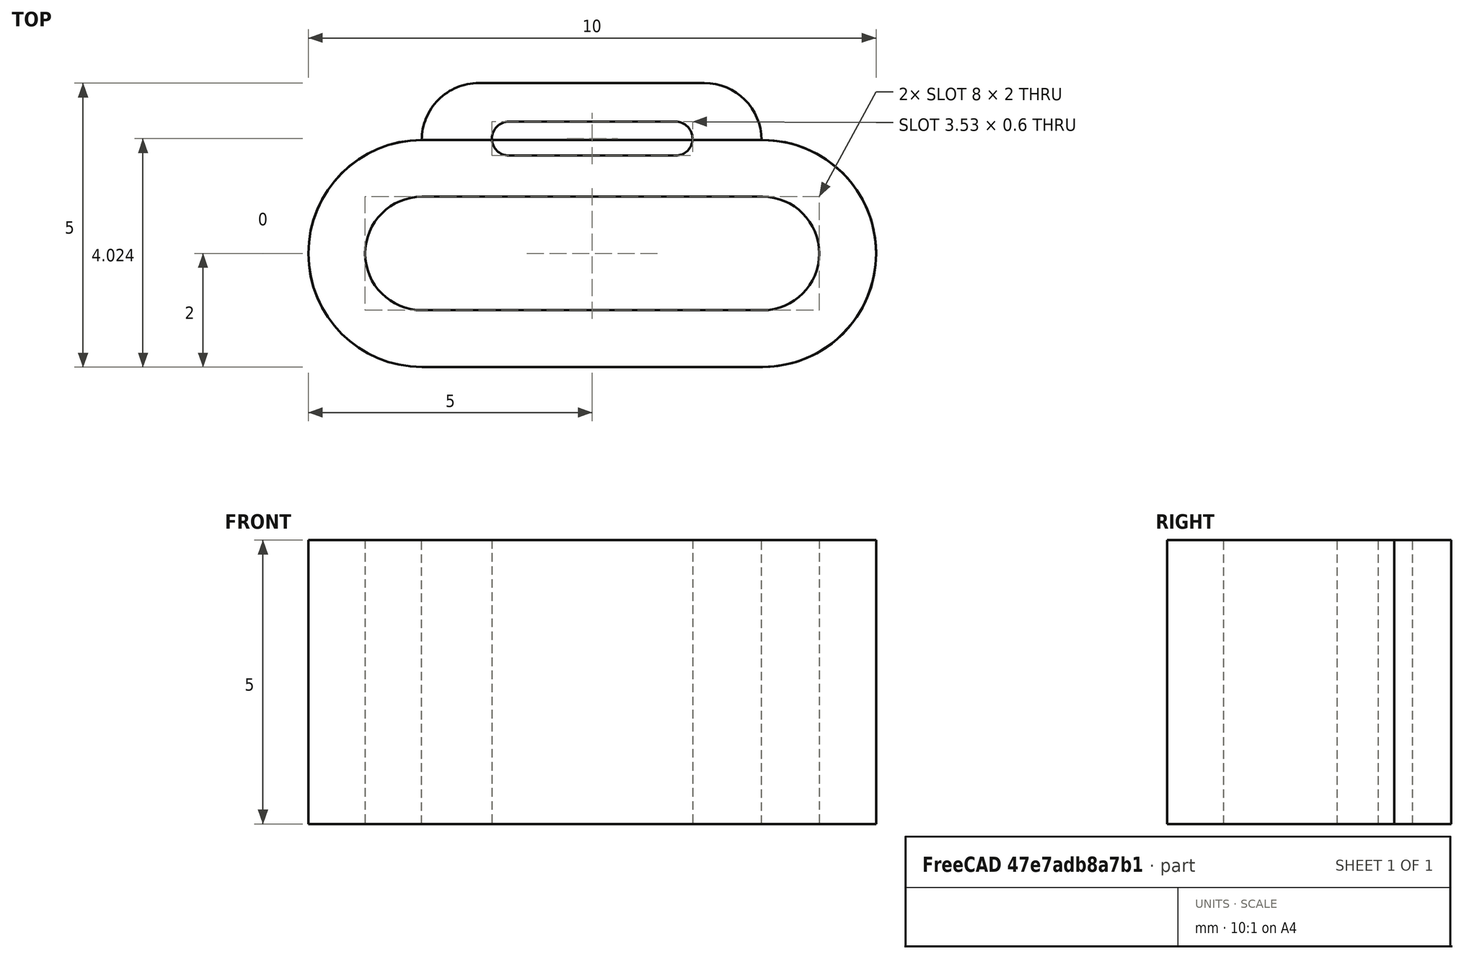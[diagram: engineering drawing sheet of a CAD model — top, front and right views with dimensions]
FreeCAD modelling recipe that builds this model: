
FCSTD DOCUMENT  (FreeCAD 2024.1R35694 (Git))
Label: strap_holder
License: Creative Commons Attribution 4.0
LicenseURL: https://creativecommons.org/licenses/by/4.0/
objects: TechDraw::DrawViewDimension×5, TechDraw::DrawProjGroupItem×3, Sketcher::SketchObject×2, PartDesign::Pad×2, PartDesign::Body×2, Spreadsheet::Sheet×1, TechDraw::DrawSVGTemplate×1, TechDraw::DrawViewImage×1, TechDraw::DrawProjGroup×1, TechDraw::DrawViewSpreadsheet×1, TechDraw::DrawPage×1
note: 15 computed .brp shape members not serialized (recipe doc carries the construction recipe); baked Part::Feature solids carry a one-line shape summary decoded from their .brp

FEATURE [Sketcher::SketchObject] Sketch
  FullyConstrained = true
  MapMode = 5
  Support = -> [XY_Plane]
  expr: Constraints[11] = <<parameters>>.hole_radius
  expr: Constraints[12] = <<parameters>>.thickness
  expr: Constraints[16] = <<parameters>>.hole_length
  sketch-geometry (8):
    g0: ArcOfCircle CenterX=-3 CenterY=0 CenterZ=0 NormalX=0 NormalY=0 NormalZ=1 AngleXU=0 Radius=1 StartAngle=1.5708 EndAngle=4.71239
    g1: ArcOfCircle CenterX=3 CenterY=1e-16 CenterZ=0 NormalX=0 NormalY=0 NormalZ=1 AngleXU=0 Radius=1 StartAngle=4.71239 EndAngle=7.85398
    g2: LineSegment StartX=-3 StartY=-1 StartZ=0 EndX=3 EndY=-1 EndZ=0
    g3: LineSegment StartX=3 StartY=1 StartZ=0 EndX=-3 EndY=1 EndZ=0
    g4: ArcOfCircle CenterX=-3 CenterY=2e-16 CenterZ=0 NormalX=0 NormalY=0 NormalZ=1 AngleXU=0 Radius=2 StartAngle=1.5708 EndAngle=4.71239
    g5: ArcOfCircle CenterX=3 CenterY=1e-16 CenterZ=0 NormalX=0 NormalY=0 NormalZ=1 AngleXU=0 Radius=2 StartAngle=4.71239 EndAngle=7.85398
    g6: LineSegment StartX=-3 StartY=-2 StartZ=0 EndX=3 EndY=-2 EndZ=0
    g7: LineSegment StartX=3 StartY=2 StartZ=0 EndX=-3 EndY=2 EndZ=0
  constraints (17):
    c: Tangent(g0,g2) = -1.5708
    c: Tangent(g2,g1) = -1.5708
    c: Tangent(g1,g3) = -1.5708
    c: Tangent(g3,g0) = -1.5708
    c: Equal(g0,g1)
    c: PointOnObject(g0,g-1)
    c: Tangent(g4,g6) = -1.5708
    c: Tangent(g6,g5) = -1.5708
    c: Tangent(g5,g7) = -1.5708
    c: Tangent(g7,g4) = -1.5708
    c: Equal(g4,g5)
    c: Radius(g0) = 1
    c: DistanceY(g1,g5) = 1
    c: Symmetric(g5,g4,g-2)
    c: Symmetric(g1,g0,g-2)
    c: Coincident(g5,g1)
    c: DistanceX(g6,g6) = 6
FEATURE [PartDesign::Pad] Pad
  Direction = (0,0,1)
  Length = 5
  Length2 = 10
  Profile = -> Sketch
  ReferenceAxis = -> Sketch [N_Axis]
  Type = 0
  expr: Length = <<parameters>>.height
FEATURE [PartDesign::Body] Body  label="single"
  Group = -> [Sketch,Pad]
  Origin = -> Origin
  Tip = -> Pad
FEATURE [Spreadsheet::Sheet] Spreadsheet  label="parameters"
  cells = A1='Parameter; B1='Value; A2='thickness; B2(thickness)==1 mm; A3='hole_radius; B3(hole_radius)==1 mm; A4='hole_length; B4(hole_length)==6 mm; A5='height; B5(height)==5 mm
FEATURE [TechDraw::DrawSVGTemplate] Template
  EditableTexts = Designed_by_Name=Dennis Wittchen; Drawing_number=1; FC-Date=Jan 17 2024; FC-SC=3:1; FC-SH=1; FC-Title=strap holder; Subtitle=modular system
  Height = 210
  Orientation = 1
  Template = /Applications/FreeCAD.app/Contents/Resources/share/Mod/TechDraw/Templates/A4_LandscapeTD.svg
  Width = 297
FEATURE [TechDraw::DrawViewImage] ActiveView
  Height = 30
  ImageFile = <userpath>/Library/Caches/FreeCAD/Cache/FreeCAD_Doc_b2a2b77d-9e3d-4a47-8089-e41d462fed02_9dbf0a_21681/PageActiveViewkthZav.png
  LockPosition = false
  Rotation = 0
  Scale = 0.3
  ScaleType = 2
  Width = 30
  X = 165.254
  Y = 128.537
FEATURE [TechDraw::DrawProjGroupItem] ProjItem  label="Front"
  CoarseView = false
  Direction = (0,-1,0)
  Focus = 100
  HardHidden = false
  IsoCount = 0
  IsoHidden = false
  IsoVisible = false
  LockPosition = true
  Perspective = false
  Rotation = 0
  RotationVector = (1,0,1e-06)
  Scale = 4
  ScaleType = 2
  ScrubCount = 0
  SeamHidden = false
  SeamVisible = false
  SmoothHidden = false
  SmoothVisible = true
  Source = -> [Body]
  Type = 0
  X = 0
  XDirection = (1,0,1e-06)
  Y = 0
FEATURE [TechDraw::DrawProjGroupItem] ProjItem001  label="Top"
  CoarseView = false
  Direction = (-1e-06,0,1)
  Focus = 100
  HardHidden = false
  IsoCount = 0
  IsoHidden = false
  IsoVisible = false
  LockPosition = false
  Perspective = false
  Rotation = 0
  RotationVector = (1,0,0)
  ScaleType = 2
  ScrubCount = 0
  SeamHidden = false
  SeamVisible = false
  SmoothHidden = false
  SmoothVisible = true
  Source = -> [Body]
  Type = 4
  X = 0
  XDirection = (1,0,1e-06)
  Y = -43
FEATURE [TechDraw::DrawProjGroupItem] ProjItem002  label="Bottom"
  CoarseView = false
  Direction = (1e-06,0,-1)
  Focus = 100
  HardHidden = false
  IsoCount = 0
  IsoHidden = false
  IsoVisible = false
  LockPosition = false
  Perspective = false
  Rotation = 0
  RotationVector = (1,0,0)
  ScaleType = 2
  ScrubCount = 0
  SeamHidden = false
  SeamVisible = false
  SmoothHidden = false
  SmoothVisible = true
  Source = -> [Body]
  Type = 5
  X = 0
  XDirection = (1,0,1e-06)
  Y = 43
FEATURE [TechDraw::DrawProjGroup] ProjGroup
  Anchor = -> ProjItem
  AutoDistribute = true
  LockPosition = false
  ProjectionType = 0
  Rotation = 0
  Scale = 4
  ScaleType = 2
  Source = -> [Body]
  Views = -> [ProjItem,ProjItem001,ProjItem002]
  X = 79.4396
  Y = 129.966
  spacingX = 25
  spacingY = 25
FEATURE [TechDraw::DrawViewDimension] Dimension
  AngleOverride = false
  Arbitrary = false
  ArbitraryTolerances = false
  EqualTolerance = true
  ExtensionAngle = 0
  FormatSpec = R%.2w
  FormatSpecOverTolerance = %+.2w
  FormatSpecUnderTolerance = %+.2w
  Inverted = false
  LineAngle = 0
  LockPosition = false
  MeasureType = 1
  OverTolerance = 0
  References2D = -> [ProjItem002]
  Rotation = 0
  ScaleType = 0
  TheoreticalExact = false
  Type = 4
  UnderTolerance = 0
  X = -28.2438
  Y = 19.9944
FEATURE [TechDraw::DrawViewDimension] Dimension001
  AngleOverride = false
  Arbitrary = false
  ArbitraryTolerances = false
  EqualTolerance = true
  ExtensionAngle = 0
  FormatSpec = %.2w
  FormatSpecOverTolerance = %+.2w
  FormatSpecUnderTolerance = %+.2w
  Inverted = false
  LineAngle = 0
  LockPosition = false
  MeasureType = 1
  OverTolerance = 0
  References2D = -> [ProjItem001]
  Rotation = 0
  ScaleType = 0
  TheoreticalExact = false
  Type = 1
  UnderTolerance = 0
  X = -0.524319
  Y = 18.8893
FEATURE [TechDraw::DrawViewDimension] Dimension002
  AngleOverride = false
  Arbitrary = false
  ArbitraryTolerances = false
  EqualTolerance = true
  ExtensionAngle = 0
  FormatSpec = %.2w
  FormatSpecOverTolerance = %+.2w
  FormatSpecUnderTolerance = %+.2w
  Inverted = false
  LineAngle = 0
  LockPosition = false
  MeasureType = 1
  OverTolerance = 0
  References2D = -> [ProjItem002]
  Rotation = 0
  ScaleType = 0
  TheoreticalExact = false
  Type = 0
  UnderTolerance = 0
  X = 26.6812
  Y = -9.61717
FEATURE [TechDraw::DrawViewDimension] Dimension003
  AngleOverride = false
  Arbitrary = false
  ArbitraryTolerances = false
  EqualTolerance = true
  ExtensionAngle = 0
  FormatSpec = %.2w
  FormatSpecOverTolerance = %+.2w
  FormatSpecUnderTolerance = %+.2w
  Inverted = false
  LineAngle = 0
  LockPosition = false
  MeasureType = 1
  OverTolerance = 0
  References2D = -> [ProjItem]
  Rotation = 0
  ScaleType = 0
  TheoreticalExact = false
  Type = 2
  UnderTolerance = 0
  X = 26.9911
  Y = 2.67476
FEATURE [TechDraw::DrawViewSpreadsheet] Sheet
  CellEnd = B5
  CellStart = A1
  Font = osifont
  LineWidth = 0.35
  LockPosition = false
  Rotation = 0
  ScaleType = 2
  Source = -> Spreadsheet
  Symbol = <blob: 2375 chars omitted>
  TextSize = 12
  X = 244.081
  Y = 126.619
FEATURE [TechDraw::DrawViewDimension] Dimension004
  AngleOverride = false
  Arbitrary = false
  ArbitraryTolerances = false
  EqualTolerance = true
  ExtensionAngle = 0
  FormatSpec = %.2w
  FormatSpecOverTolerance = %+.2w
  FormatSpecUnderTolerance = %+.2w
  Inverted = false
  LineAngle = 0
  LockPosition = false
  MeasureType = 1
  OverTolerance = 0
  References2D = -> [ProjItem]
  Rotation = 0
  ScaleType = 0
  TheoreticalExact = false
  Type = 1
  UnderTolerance = 0
  X = -1.0067
  Y = 19.151
FEATURE [TechDraw::DrawPage] Page  label="documentation"
  KeepUpdated = true
  NextBalloonIndex = 1
  ProjectionType = 0
  Template = -> Template
  Views = -> [ActiveView,ProjGroup,Dimension,Dimension001,Dimension002,Dimension003,Sheet,Dimension004]
FEATURE [Sketcher::SketchObject] Sketch001
  FullyConstrained = false
  MapMode = 5
  Support = -> [XY_Plane001]
  expr: Constraints[13] = <<parameters>>.hole_length
  expr: Constraints[9] = <<parameters>>.hole_radius
  sketch-geometry (14):
    g0: ArcOfCircle CenterX=-3 CenterY=0 CenterZ=0 NormalX=0 NormalY=0 NormalZ=1 AngleXU=0 Radius=1 StartAngle=1.5708 EndAngle=4.71239
    g1: ArcOfCircle CenterX=3 CenterY=0 CenterZ=0 NormalX=0 NormalY=0 NormalZ=1 AngleXU=0 Radius=1 StartAngle=4.71239 EndAngle=7.85398
    g2: LineSegment StartX=-3 StartY=-1 StartZ=0 EndX=3 EndY=-1 EndZ=0
    g3: LineSegment StartX=3 StartY=1 StartZ=0 EndX=-3 EndY=1 EndZ=0
    g4: ArcOfCircle CenterX=-3 CenterY=1e-16 CenterZ=0 NormalX=0 NormalY=0 NormalZ=1 AngleXU=0 Radius=1.99883 StartAngle=1.5722 EndAngle=4.71239
    g5: ArcOfCircle CenterX=3 CenterY=0 CenterZ=0 NormalX=0 NormalY=0 NormalZ=1 AngleXU=0 Radius=1.99883 StartAngle=4.71239 EndAngle=7.86247
    g6: LineSegment StartX=-3 StartY=-1.99883 StartZ=0 EndX=3 EndY=-1.99883 EndZ=0
    g7: ArcOfCircle CenterX=-1.46614 CenterY=2.02372 CenterZ=0 NormalX=0 NormalY=0 NormalZ=1 AngleXU=0 Radius=0.3 StartAngle=1.5708 EndAngle=4.71239
    g8: ArcOfCircle CenterX=1.46614 CenterY=2.02372 CenterZ=0 NormalX=0 NormalY=0 NormalZ=1 AngleXU=0 Radius=0.3 StartAngle=4.71239 EndAngle=7.85398
    g9: LineSegment StartX=-1.46614 StartY=2.32372 StartZ=0 EndX=1.46614 EndY=2.32372 EndZ=0
    g10: LineSegment StartX=-1.46614 StartY=1.72372 StartZ=0 EndX=1.46614 EndY=1.72372 EndZ=0
    g11: ArcOfCircle CenterX=-2 CenterY=2.00024 CenterZ=0 NormalX=0 NormalY=0 NormalZ=1 AngleXU=0 Radius=1.00281 StartAngle=1.5708 EndAngle=3.143
    g12: LineSegment StartX=-2 StartY=3.00306 StartZ=0 EndX=1.97343 EndY=3.00306 EndZ=0
    g13: ArcOfCircle CenterX=1.97343 CenterY=1.99343 CenterZ=0 NormalX=0 NormalY=0 NormalZ=1 AngleXU=0 Radius=1.00963 StartAngle=0.00527808 EndAngle=1.5708
  constraints (26):
    c: Tangent(g0,g2) = -1.5708
    c: Tangent(g2,g1) = -1.5708
    c: Tangent(g1,g3) = -1.5708
    c: Tangent(g3,g0) = -1.5708
    c: Equal(g0,g1)
    c: PointOnObject(g0,g-1)
    c: Tangent(g4,g6) = -1.5708
    c: Tangent(g6,g5) = -1.5708
    c: Equal(g4,g5)
    c: Radius(g0) = 1
    c: Symmetric(g5,g4,g-2)
    c: Symmetric(g1,g0,g-2)
    c: Coincident(g5,g1)
    c: DistanceX(g6,g6) = 6
    c: Tangent(g7,g9) = 1.5708
    c: Tangent(g7,g10) = -1.5708
    c: Tangent(g8,g9) = 1.5708
    c: Tangent(g8,g10) = -1.5708
    c: Equal(g7,g8)
    c: Radius(g7) = 0.3
    c: Symmetric(g7,g8,g-2)
    c: Perpendicular(g4,g11) = 1.5708
    c: Tangent(g11,g12) = 1.5708
    c: Tangent(g12,g13) = 1.5708
    c: Coincident(g13,g5)
    c: Horizontal(g12)
FEATURE [PartDesign::Pad] Pad001
  Direction = (0,0,1)
  Length = 5
  Length2 = 10
  Profile = -> Sketch001
  ReferenceAxis = -> Sketch001 [N_Axis]
  Refine = true
  Type = 0
  expr: Length = <<parameters>>.height
FEATURE [PartDesign::Body] Body001  label="double"
  Group = -> [Sketch001,Pad001]
  Origin = -> Origin001
  Tip = -> Pad001
